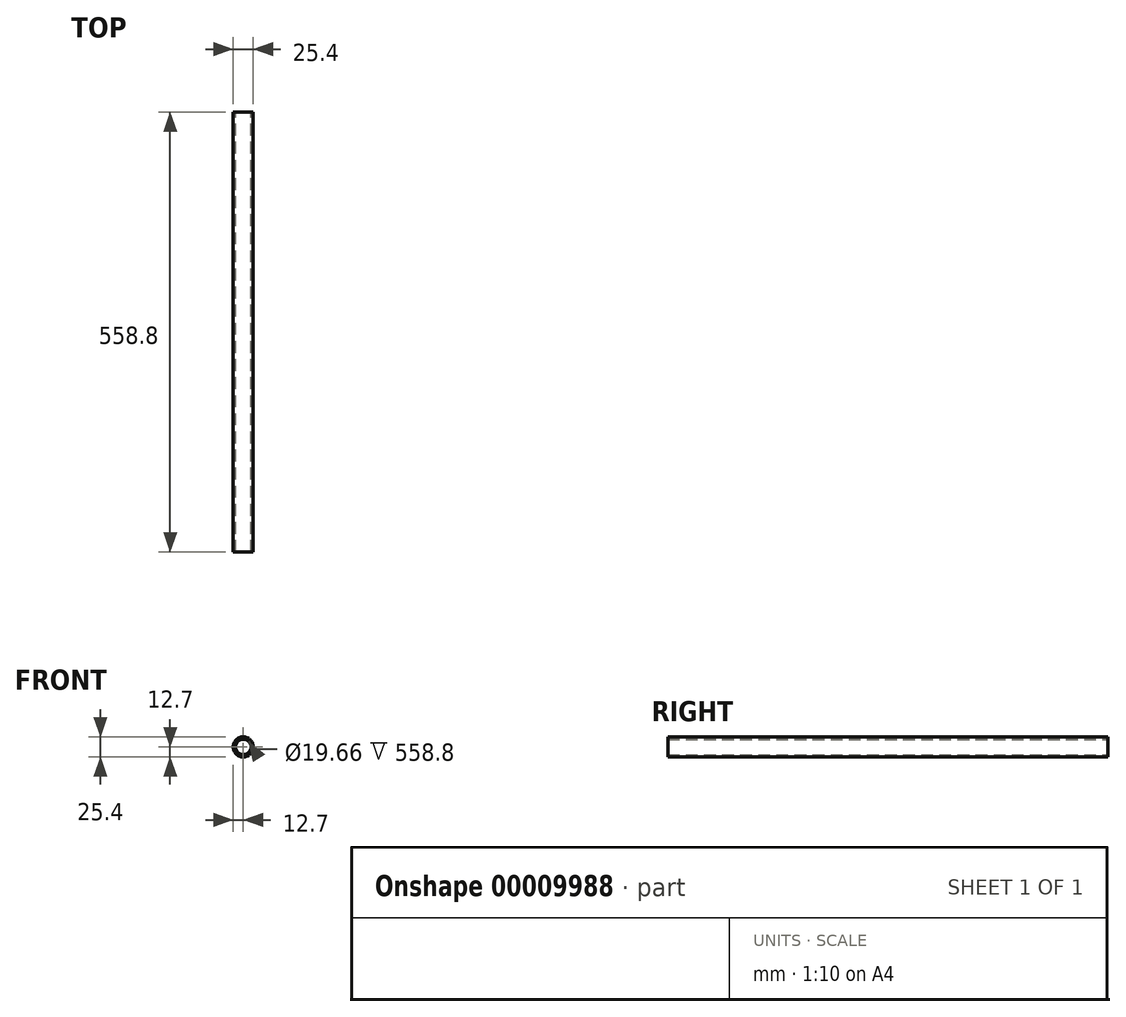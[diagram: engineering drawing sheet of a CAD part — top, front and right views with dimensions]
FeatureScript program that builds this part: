
annotation { "Feature Type Name" : "Feature", "Feature Type Description" : "" }
export const myFeature = defineFeature(function(context is Context, id is Id, definition is map)
    precondition{}
    {
        {
            var Q0;
            Q0=qCreatedBy(makeId("Front.planeOp"),FACE);
            var sketch = newSketch(context, id + "F0", { "sketchPlane" : qUnion([Q0])});
            skCircle(sketch, "E0", {"center": v(0, 0) * mm, "radius": 12.7 * mm});
            skCircle(sketch, "E1", {"center": v(0, 0) * mm, "radius": 9.83 * mm});
            skSolve(sketch);
        }
        {
            var Q0;
            Q0=qSketchRegion(id+"F0",true);
            extrude(context, id + "F1", {"entities" : qUnion([Q0]), "depth" : 558.8 * mm});
        }
    });
